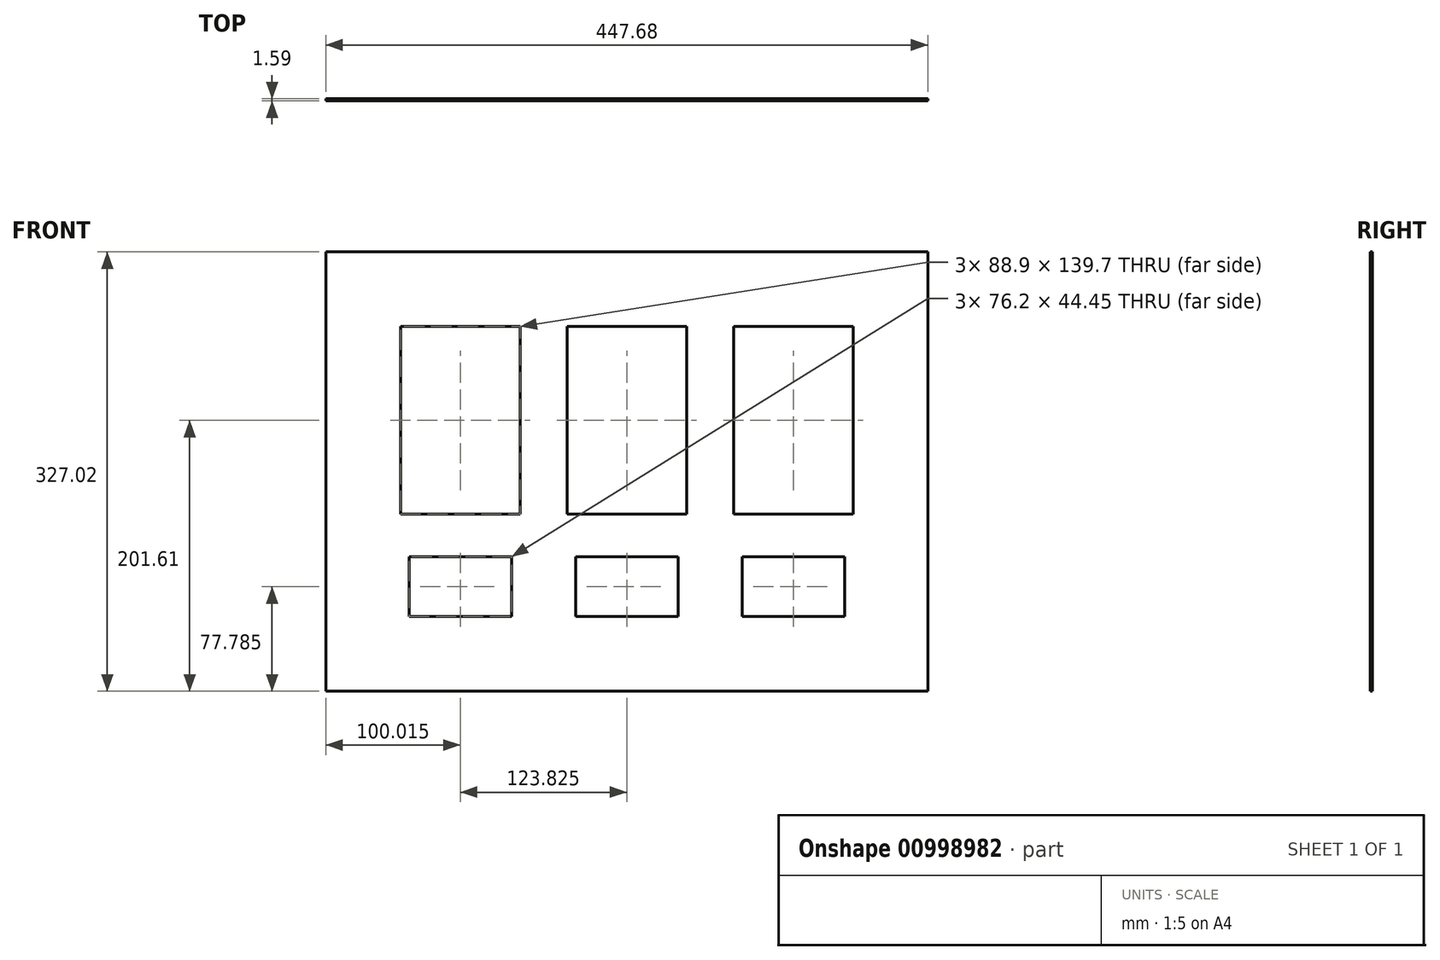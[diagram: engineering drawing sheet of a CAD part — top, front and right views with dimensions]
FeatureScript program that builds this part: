
annotation { "Feature Type Name" : "Feature", "Feature Type Description" : "" }
export const myFeature = defineFeature(function(context is Context, id is Id, definition is map)
    precondition{}
    {
        {
            var Q0;
            Q0=qCreatedBy(makeId("Front.planeOp"),FACE);
            var sketch = newSketch(context, id + "F0", { "sketchPlane" : qUnion([Q0])});
            skLineSegment(sketch, "E0.bottom", {"start": v(223.84, -163.51) * mm, "end": v(-223.84, -163.51) * mm});
            skLineSegment(sketch, "E0.top", {"start": v(223.84, 163.51) * mm, "end": v(-223.84, 163.51) * mm});
            skLineSegment(sketch, "E0.left", {"start": v(223.84, -163.51) * mm, "end": v(223.84, 163.51) * mm});
            skLineSegment(sketch, "E0.right", {"start": v(-223.84, -163.51) * mm, "end": v(-223.84, 163.51) * mm});
            skPoint(sketch, "E0.middle", {"position": v(0, 0) * mm});
            skLineSegment(sketch, "E1.bottom", {"start": v(-168.28, 107.95) * mm, "end": v(-79.38, 107.95) * mm});
            skLineSegment(sketch, "E1.top", {"start": v(-168.28, -31.75) * mm, "end": v(-79.38, -31.75) * mm});
            skLineSegment(sketch, "E1.left", {"start": v(-168.28, 107.95) * mm, "end": v(-168.28, -31.75) * mm});
            skLineSegment(sketch, "E1.right", {"start": v(-79.38, 107.95) * mm, "end": v(-79.38, -31.75) * mm});
            skLineSegment(sketch, "E2.MirrorCS", {"start": v(168.28, -31.75) * mm, "end": v(79.38, -31.75) * mm});
            skLineSegment(sketch, "E3.bottom", {"start": v(-44.45, -31.75) * mm, "end": v(44.45, -31.75) * mm});
            skLineSegment(sketch, "E3.top", {"start": v(-44.45, 107.95) * mm, "end": v(44.45, 107.95) * mm});
            skLineSegment(sketch, "E3.left", {"start": v(-44.45, -31.75) * mm, "end": v(-44.45, 107.95) * mm});
            skLineSegment(sketch, "E3.right", {"start": v(44.45, -31.75) * mm, "end": v(44.45, 107.95) * mm});
            skLineSegment(sketch, "E4.bottom", {"start": v(-85.73, -63.5) * mm, "end": v(-161.93, -63.5) * mm});
            skLineSegment(sketch, "E4.top", {"start": v(-85.73, -107.95) * mm, "end": v(-161.93, -107.95) * mm});
            skLineSegment(sketch, "E4.left", {"start": v(-85.73, -63.5) * mm, "end": v(-85.73, -107.95) * mm});
            skLineSegment(sketch, "E4.right", {"start": v(-161.93, -63.5) * mm, "end": v(-161.93, -107.95) * mm});
            skPoint(sketch, "E4.middle", {"position": v(-123.83, -85.73) * mm});
            skPoint(sketch, "E4.middle.positionSnap0", {"position": v(-123.83, -31.75) * mm});
            skPoint(sketch, "E4.centerSnap0", {"position": v(-123.83, -31.75) * mm});
            skLineSegment(sketch, "E5.MirrorCS", {"start": v(85.73, -63.5) * mm, "end": v(85.73, -107.95) * mm});
            skLineSegment(sketch, "E6.MirrorCS", {"start": v(85.73, -63.5) * mm, "end": v(161.93, -63.5) * mm});
            skLineSegment(sketch, "E7.MirrorCS", {"start": v(161.93, -63.5) * mm, "end": v(161.93, -107.95) * mm});
            skLineSegment(sketch, "E8.MirrorCS", {"start": v(85.73, -107.95) * mm, "end": v(161.93, -107.95) * mm});
            skPoint(sketch, "E9.middle", {"position": v(0, -85.73) * mm});
            skLineSegment(sketch, "E10", {"start": v(-260.01, 107.95) * mm, "end": v(263.4, 107.95) * mm, "construction": true});
            skLineSegment(sketch, "E11", {"start": v(79.38, -31.75) * mm, "end": v(79.38, 107.95) * mm});
            skLineSegment(sketch, "E12", {"start": v(168.28, -31.75) * mm, "end": v(168.28, 107.95) * mm});
            skPoint(sketch, "E12.endSnap0", {"position": v(1.7, 107.95) * mm});
            skLineSegment(sketch, "E13", {"start": v(168.28, 107.95) * mm, "end": v(79.38, 107.95) * mm});
            skLineSegment(sketch, "E14.bottom", {"start": v(-38.1, -107.95) * mm, "end": v(38.1, -107.95) * mm});
            skLineSegment(sketch, "E14.top", {"start": v(-38.1, -63.5) * mm, "end": v(38.1, -63.5) * mm});
            skLineSegment(sketch, "E14.left", {"start": v(-38.1, -107.95) * mm, "end": v(-38.1, -63.5) * mm});
            skLineSegment(sketch, "E14.right", {"start": v(38.1, -107.95) * mm, "end": v(38.1, -63.5) * mm});
            skSolve(sketch);
        }
        {
            var Q0;
            Q0=makeQuery(id+"F0.imprint","IMPRINT",FACE,{"disambiguationData":[TD([[makeQuery(id+"F0.imprint","IMPRINT",EDGE,{"derivedFrom":sQuery(id+"F0.wireOp",EDGE,"E0.bottom")}),-1.0]])]});
            extrude(context, id + "F1", {"entities" : qUnion([Q0]), "depth" : 1.59 * mm, "offsetDistance" : 25.4 * mm});
        }
    });
